# Revit family: Haworth_Patterns_StudioTable
name_source: partatom
category: Furniture Systems
revit_build: Autodesk Revit 2018 (Build: 20170223_1515(x64)
units: mm (PartAtom-declared; Revit-internal decimal feet)

## family parameters
Always vertical = Yes
Cut with Voids When Loaded = No
OmniClass Number = 23.40.70.14.64.21
OmniClass Title = Systems Furniture
Part Type = Normal
Room Calculation Point = No
Round Connector Dimension = Use Diameter
Shared = No
Work Plane-Based = No

## types (6) — shared parameters
Actual Depth = 30"
Actual Height = 29"
Assembly Code = E2020200
Bench Finish = Haworth _ Wood _ White Oak
Custom Size = No
Description = Haworth - Patterns - Studio Table
Flip Top Finish = Haworth _ Paint _ Metallic Champagne
Manufacturer = Haworth
Max. Depth = 63"
Max. Width = 249"
Min. Depth = 30"
Min. Width = 78"
Model = Haworth - Patterns - Studio Table
Revision Number = 4
Size = Verify Final Dim. w/ Haworth
Standard Depths = 30 in.
Standard Width = 78, 102, 126, 153, 201, 249 in.
Sustainability Info = http://www.haworth.com
URL = https://www.haworth.com
URL - Product = https://www.haworth.com
Warranty = http://www.haworth.com

## per-type parameters (varying)
| type | Actual Width | Flip Top One | Flip Top Two | One Piece | One Piece Width | Two Piece | Two Piece Width | Width |
| 78w | 78" | Yes | Yes | Yes | 72" | No | 34 1/2" | 78" |
| 102w | 102" | No | No | Yes | 96" | No | 46 1/2" | 102" |
| 126w | 126" | No | No | Yes | 120" | No | 58 1/2" | 126" |
| 153w | 153" | No | No | No | 147" | Yes | 72" | 153" |
| 201w | 201" | No | No | No | 195" | Yes | 96" | 201" |
| 249w | 249" | No | No | No | 243" | Yes | 120" | 249" |

## geometry (parser evidence)
native form markers: Sweep x11
no freeform markers — native parametric forms only
